# Revit family: Deca_Misturador de mesa para cozinha_Fast_1256.59
name_source: partatom
category: Plumbing Fixtures
units: mm (PartAtom-declared; Revit-internal decimal feet)

## family parameters
Cut with Voids When Loaded = No
Host = Face
Part Type = Normal
Room Calculation Point = No
Round Connector Dimension = Use Radius
Shared = Yes

## types (1)
- 1256.C59_Cromado
    Acompanha o Produto = -
    Aprovado por = quattroD
    Atendimento ao Cliente = 0800-0117073
    CWFU = 0
    Categoria = METAIS PARA COZINHA
    Composição Anel Vedação = -
    Composição Assento = -
    Composição Básica = Liga de Cobre (bronze e latão),Plásticos de Engenharia,Elastômeros
    Composição Componente = -
    Consumo = -
    Cor Interna = -
    Cor Principal = Cromado
    Cor Secundária = -
    Cores Componente = -
    Criado por = quattroD
    Código Pai = 1256.59
    Default Elevation = 0 mm  [stored 0 ft]
    Description = Misturador de mesa para cozinha
    Diâmetro Água Fria = 15 mm  [stored 0.0492126 ft]
    Diâmetro Água Quente = 15 mm  [stored 0.0492126 ft]
    HWFU = 0
    Informações Complementares = -
    Itens de Instalação = -
    Linha = Fast
    Manufacturer = Deca
    Material = Deca_Cromado
    Model = 1256.C59
    Norma = NBR16749
    Peso Líquido (Kg) = 2.137
    Pressão máx. funcionamento = 40 MCA
    Pressão mín. Aquec. Acúmulo = -
    Pressão mín. Aquec. Passagem = -
    Pressão mín. funcionamento = 2 MCA
    Raio Água Fria = 8 mm  [stored 0.0262467 ft]
    Raio Água Quente = 8 mm  [stored 0.0262467 ft]
    Saída de Esgoto = -
    Segmento = Banheiro Médio
    Tipo de dispositivo economizador = Não
    Tipo de mecanismo utilizado = MVC -1/4 volta
    Tipo de rosca de entrada = BSP NBR 8133
    Tipo de rosca de saída = -
    URL = www.deca.com.br
    Vazão na Pressão máx. (L/min) = 16
    Vazão na Pressão mín. (L/min) = 5

note: source unit labels omitted for Vazão na Pressão máx. (L/min), Vazão na Pressão mín. (L/min) — the stored unit's dimension contradicts the parameter name (converter mislabeling)

note: [stored X ft] marks values corroborated as IEEE doubles in the binary element streams (Revit-internal decimal feet)

## geometry (parser evidence)
native form markers: Sweep x1
no freeform markers — native parametric forms only
